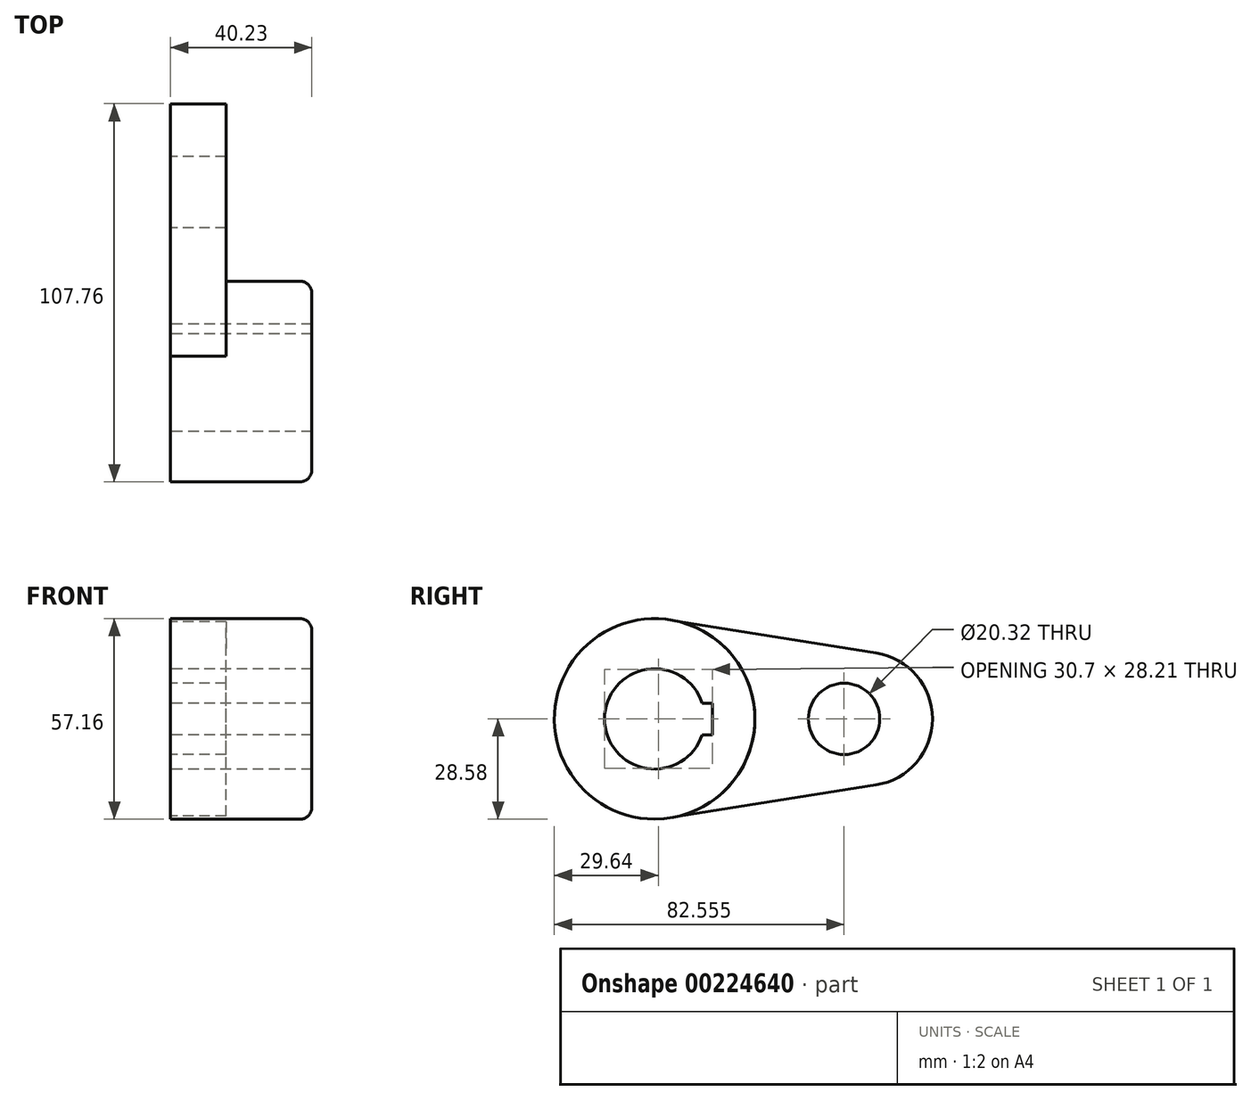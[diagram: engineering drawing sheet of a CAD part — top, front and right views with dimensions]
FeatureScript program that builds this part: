
annotation { "Feature Type Name" : "Feature", "Feature Type Description" : "" }
export const myFeature = defineFeature(function(context is Context, id is Id, definition is map)
    precondition{}
    {
        {
            var Q0;
            Q0=qCreatedBy(makeId("Right.planeOp"),FACE);
            var sketch = newSketch(context, id + "F0", { "sketchPlane" : qUnion([Q0])});
            skCircle(sketch, "E0", {"center": v(0, 0) * mm, "radius": 14.29 * mm});
            skCircle(sketch, "E1", {"center": v(0, 0) * mm, "radius": 28.58 * mm});
            skCircle(sketch, "E2", {"center": v(53.98, 0) * mm, "radius": 10.16 * mm});
            skLineSegment(sketch, "E3", {"start": v(7.18, 27.66) * mm, "end": v(63.1, 18.82) * mm});
            skLineSegment(sketch, "E4", {"start": v(7.18, -27.66) * mm, "end": v(63.1, -18.82) * mm});
            skArc(sketch, "E5", {"start": v(63.1, 18.82) * mm, "mid": v(79.18, 0) * mm, "end": v(63.1, -18.82) * mm});
            skLineSegment(sketch, "E6.bottom", {"start": v(16.4, -4.5) * mm, "end": v(13.56, -4.5) * mm});
            skLineSegment(sketch, "E6.top", {"start": v(16.4, 4.5) * mm, "end": v(13.56, 4.5) * mm});
            skLineSegment(sketch, "E6.left", {"start": v(16.4, -4.5) * mm, "end": v(16.4, 4.5) * mm});
            skSolve(sketch);
        }
        {
            var Q0;
            {var subQ0=sQuery(id+"F0.wireOp",EDGE,"E6.bottom");Q0=makeQuery(id+"F0.imprint","IMPRINT",FACE,{"disambiguationData":[TD([[makeQuery(id+"F0.imprint","IMPRINT",EDGE,{"derivedFrom":subQ0}),1.0]])]});}
            extrude(context, id + "F1", {"entities" : qUnion([Q0]), "depth" : 40.23 * mm});
        }
        {
            var Q0;
            Q0 = qSketchRegion(id + "F0", true);
            extrude(context, id + "F2", {"entities" : qUnion([Q0]), "operationType" : NewBodyOperationType.ADD, "depth" : 15.77 * mm});
        }
        {
            var Q0;
            Q0=makeQuery(id+"F1.opExtrude","CAP_EDGE",EDGE,{"disambiguationData":[OSD([sQuery(id+"F0.wireOp",EDGE,"E1")])],"isStart":false});
            fillet(context, id + "F3", {"entities" : qUnion([Q0]), "radius" : 3.3 * mm, "tangentPropagation" : true, "allowEdgeOverflow" : false});
        }
    });
